# Revit family: QF_ELECTROLUXPROFESSIONAL_603914_HSG3RPFSE3
name_source: partatom
category: Specialty Equipment
units: mm (PartAtom-declared; Revit-internal decimal feet)

## family parameters
Always vertical = Yes
Cut with Voids When Loaded = No
Enable Cutting in Views = No
Maintain Annotation Orientation = No
Part Type = Normal
Room Calculation Point = No
Round Connector Dimension = Use Diameter
Shared = Yes
Work Plane-Based = No

## types (1)
- Standard
    Accessory = No
    Cold Water Size = 0"
    Compressed Air Pressure = 0.00 psi
    Compressed Air Size = 0"
    Compressed Air Volume = 0 GPM
    Condensate Return Size = 0"
    Cycle = 50 Hz
    Default Elevation = 0 mm  [stored 0 ft]
    Depth Actual = 683 mm  [stored 2.24081 ft]
    Description = SPEEDELIGHT FLEX, FLAT RTP, 400V
    Direct Waste Size = 0"
    Gas Input Pressure = 0.0
    Gas KW = 0
    Gas Size = 0"
    HP = 6.7 HP
    Height Actual = 619 mm
    Hot Water Size = 0"
    Item Number = 603914
    Length Actual = 370 mm  [stored 1.21391 ft]
    Manufacturer = Electrolux Professional
    Model = HSG3RPFSE3
    Phase = 3
    Refrigerant Compressor Remote = Yes
    Refrigeration Liquid Line Size = 0 mm  [stored 0 ft]
    Refrigeration Suction Line Size = 0 mm  [stored 0 ft]
    Steam Consumption per Hour = 0
    Steam Supply Maximum Pressure = 0.00 psi
    Steam Supply Minimum Pressure = 0.00 psi
    Steam Supply Size = 0"
    URL = http://www.electroluxprofessional.com
    URL Manufacturer = http://www.electroluxprofessional.com
    Volts = 380 V
    Watts = 0 W
    Weight = 47.00 lbm

note: source unit labels omitted for Gas Input Pressure — the stored unit's dimension contradicts the parameter name (converter mislabeling)

note: [stored X ft] marks values corroborated as IEEE doubles in the binary element streams (Revit-internal decimal feet)

## geometry (parser evidence)
native form markers: Sweep x3
no freeform markers — native parametric forms only
